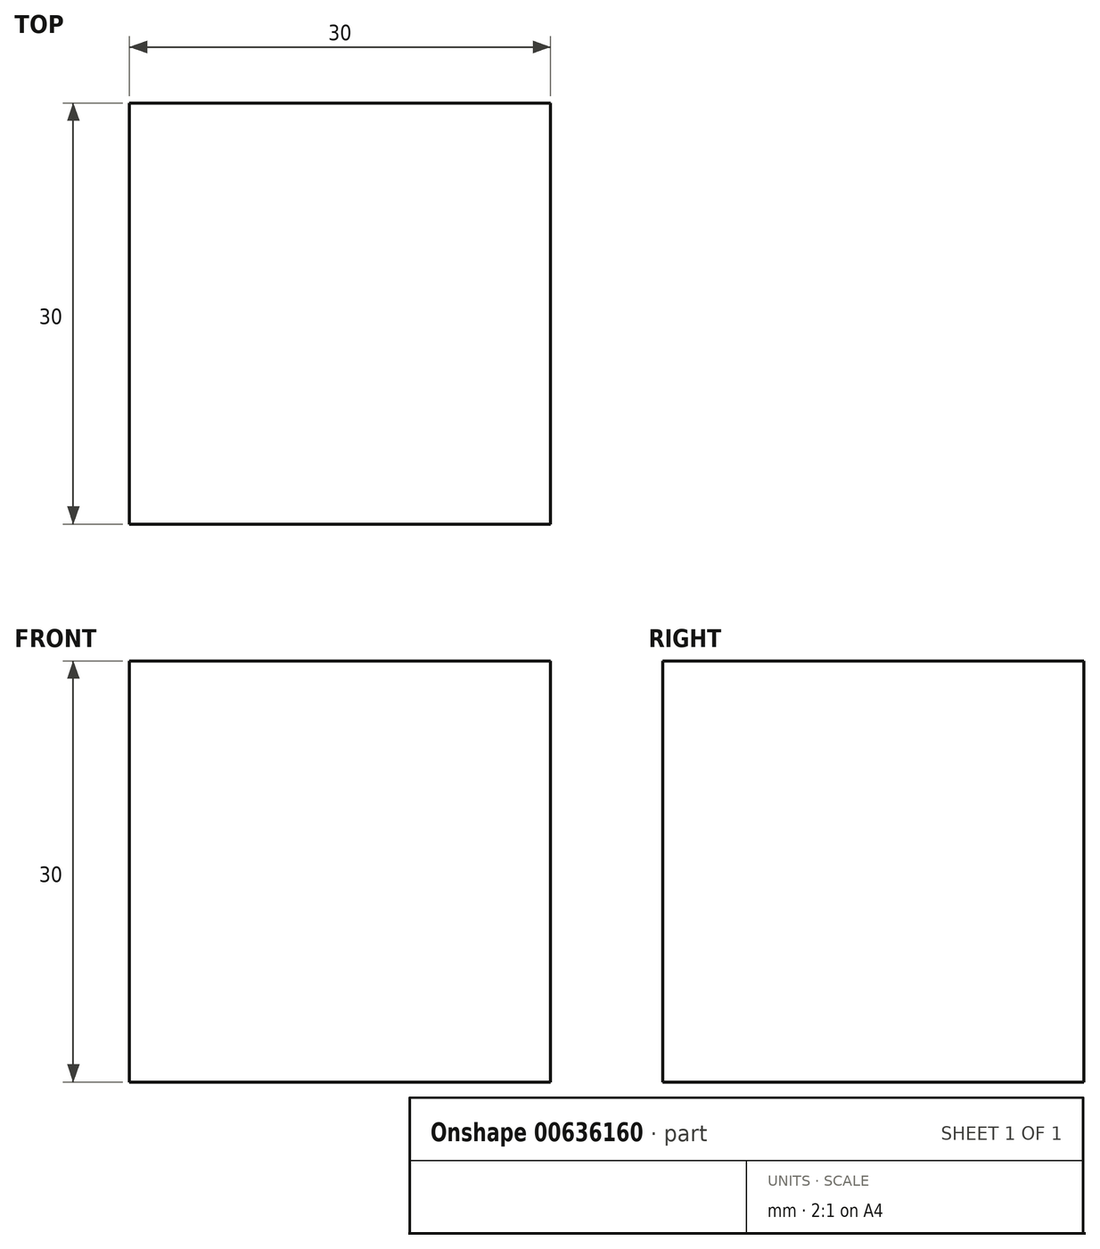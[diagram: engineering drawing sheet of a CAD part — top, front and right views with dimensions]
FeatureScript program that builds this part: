
annotation { "Feature Type Name" : "Feature", "Feature Type Description" : "" }
export const myFeature = defineFeature(function(context is Context, id is Id, definition is map)
    precondition{}
    {
        {
            var Q0;
            Q0=qCreatedBy(makeId("Top.planeOp"),FACE);
            var sketch = newSketch(context, id + "F0", { "sketchPlane" : qUnion([Q0])});
            skLineSegment(sketch, "E0.bottom", {"start": v(-25.16, 18.08) * mm, "end": v(4.84, 18.08) * mm});
            skLineSegment(sketch, "E0.top", {"start": v(-25.16, -11.92) * mm, "end": v(4.84, -11.92) * mm});
            skLineSegment(sketch, "E0.left", {"start": v(-25.16, 18.08) * mm, "end": v(-25.16, -11.92) * mm});
            skLineSegment(sketch, "E0.right", {"start": v(4.84, 18.08) * mm, "end": v(4.84, -11.92) * mm});
            skSolve(sketch);
        }
        {
            var Q0;
            Q0=makeQuery(id+"F0.imprint","IMPRINT",FACE,{"disambiguationData":[TD([[makeQuery(id+"F0.imprint","IMPRINT",EDGE,{"derivedFrom":sQuery(id+"F0.wireOp",EDGE,"E0.bottom")}),-1.0]])]});
            extrude(context, id + "F1", {"entities" : qUnion([Q0]), "depth" : 30 * mm, "offsetDistance" : 25 * mm});
        }
    });
